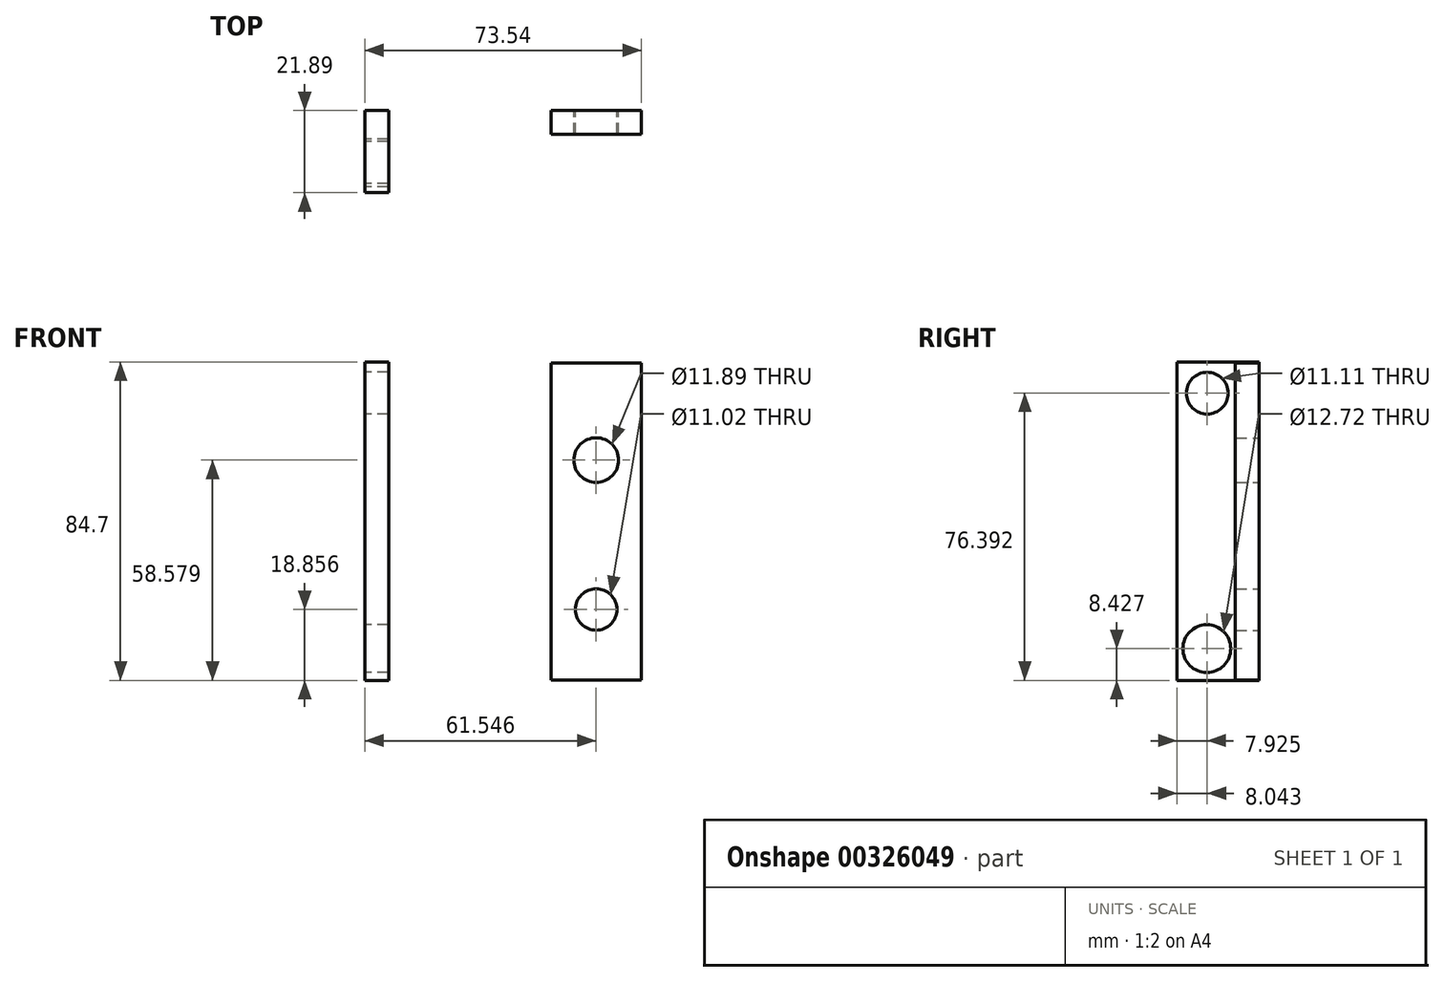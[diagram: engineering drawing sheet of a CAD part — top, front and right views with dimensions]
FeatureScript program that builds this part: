
annotation { "Feature Type Name" : "Feature", "Feature Type Description" : "" }
export const myFeature = defineFeature(function(context is Context, id is Id, definition is map)
    precondition{}
    {
        {
            var Q0;
            Q0=qCreatedBy(makeId("Front.planeOp"),FACE);
            var sketch = newSketch(context, id + "F0", { "sketchPlane" : qUnion([Q0])});
            skLineSegment(sketch, "E0.bottom", {"start": v(49.55, -7.29) * mm, "end": v(73.54, -7.29) * mm});
            skLineSegment(sketch, "E0.top", {"start": v(49.55, -91.6) * mm, "end": v(73.54, -91.6) * mm});
            skLineSegment(sketch, "E0.left", {"start": v(49.55, -7.29) * mm, "end": v(49.55, -91.6) * mm});
            skLineSegment(sketch, "E0.right", {"start": v(73.54, -7.29) * mm, "end": v(73.54, -91.6) * mm});
            skPoint(sketch, "E1", {"position": v(61.55, -7.29) * mm});
            skCircle(sketch, "E2", {"center": v(61.55, -33.1) * mm, "radius": 5.94 * mm});
            skCircle(sketch, "E3", {"center": v(61.55, -72.82) * mm, "radius": 5.51 * mm});
            skPoint(sketch, "E3.centerSnap0", {"position": v(61.55, -91.6) * mm});
            skSolve(sketch);
        }
        {
            var Q0;
            Q0 = qSketchRegion(id + "F0", true);
            extrude(context, id + "F1", {"entities" : qUnion([Q0]), "depth" : 6.35 * mm});
        }
        {
            var Q0;
            Q0=qCreatedBy(makeId("Right.planeOp"),FACE);
            var sketch = newSketch(context, id + "F2", { "sketchPlane" : qUnion([Q0])});
            skLineSegment(sketch, "E4.bottom", {"start": v(0, -6.98) * mm, "end": v(-21.9, -6.98) * mm});
            skLineSegment(sketch, "E4.top", {"start": v(0, -91.68) * mm, "end": v(-21.9, -91.68) * mm});
            skLineSegment(sketch, "E4.left", {"start": v(0, -6.98) * mm, "end": v(0, -91.68) * mm});
            skLineSegment(sketch, "E4.right", {"start": v(-21.9, -6.98) * mm, "end": v(-21.9, -91.68) * mm});
            skPoint(sketch, "E5", {"position": v(-10.95, -6.98) * mm});
            skPoint(sketch, "E6", {"position": v(-16.54, -6.98) * mm});
            skPoint(sketch, "E7", {"position": v(-10.95, -91.68) * mm});
            skCircle(sketch, "E8", {"center": v(-13.85, -15.29) * mm, "radius": 5.55 * mm});
            skCircle(sketch, "E9", {"center": v(-13.97, -83.25) * mm, "radius": 6.36 * mm});
            skSolve(sketch);
        }
        {
            var Q0;
            Q0 = qSketchRegion(id + "F2", true);
            extrude(context, id + "F3", {"entities" : qUnion([Q0]), "depth" : 6.35 * mm});
        }
    });
